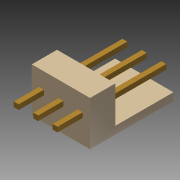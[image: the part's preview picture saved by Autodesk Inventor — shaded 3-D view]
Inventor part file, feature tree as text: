
AUTODESK INVENTOR PART (.ipt)
format: ipt  version: 2015 (Build 190159000, 159)  size: 156,160 bytes
history: native  units: mm
features: extrude x4, sketch x4
ambient origin geometry x8: Origin, YZ Plane, XZ Plane, XY Plane, X Axis, Y Axis, Z Axis, Center Point
bodies: Volumenkörper1 (feature_tree)
feature tree (8):
  extrude  "Extrusion1"  Depth=3.3mm
  extrude  "Extrusion2"  Depth=1.0mm
  extrude  "Extrusion3"  Depth=0.64mm
  extrude  "Extrusion4"  Depth=0.64mm
  sketch  "Skizze1"  dims[d0=7.62mm d1=3.3mm]
  sketch  "Skizze2"  dims[d2=5.8mm d3=0.0mm d4=1.0mm]
  sketch  "Skizze3"  dims[d5=7.6mm d6=0.0mm d7=0.64mm]
  sketch  "Skizze4"  dims[d8=0.64mm d9=0.64mm d10=0.64mm d11=0.64mm d12=0.64mm d13=7.62mm d15=1.9mm d16=1.9mm d17=0.95mm d18=0.95mm d19=4.8mm d20=2.08mm d21=7.6mm d22=0.0mm d23=0.64mm d24=0.64mm d25=0.64mm d26=0.64mm d27=0.64mm d28=0.64mm d29=0.95mm d30=0.95mm d31=1.9mm d32=1.9mm d33=2.08mm d34=2.08mm d35=2.08mm d36=3.3mm d37=0.0mm]
